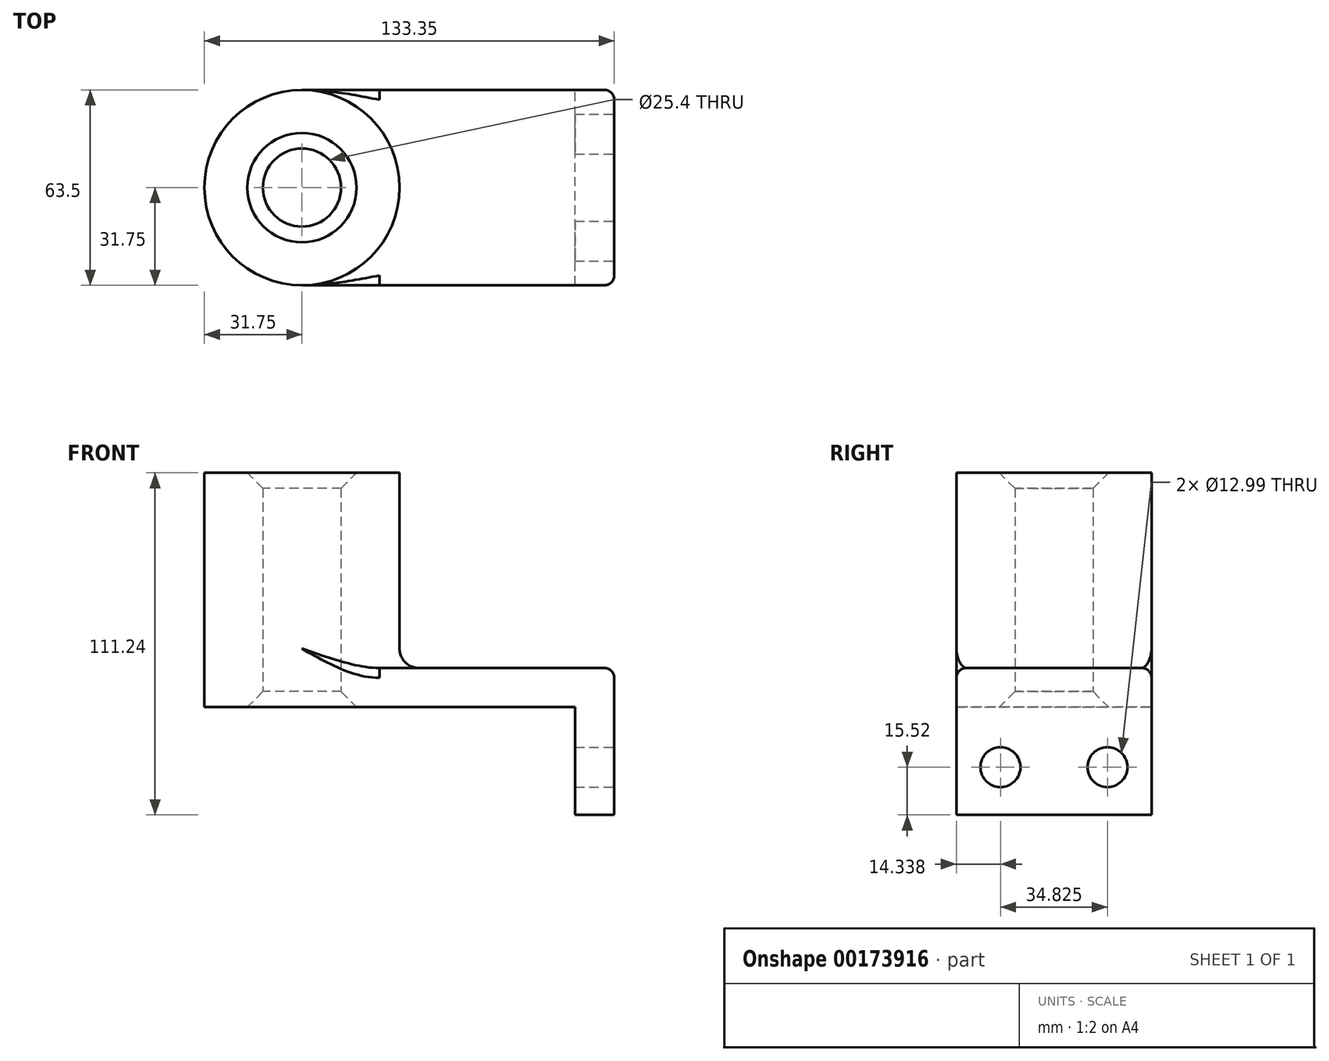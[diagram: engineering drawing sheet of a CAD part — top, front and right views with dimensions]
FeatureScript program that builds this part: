
annotation { "Feature Type Name" : "Feature", "Feature Type Description" : "" }
export const myFeature = defineFeature(function(context is Context, id is Id, definition is map)
    precondition{}
    {
        {
            var Q0;
            Q0=qCreatedBy(makeId("Top.planeOp"),FACE);
            var sketch = newSketch(context, id + "F0", { "sketchPlane" : qUnion([Q0])});
            skLineSegment(sketch, "E0.bottom", {"start": v(-50.8, 31.75) * mm, "end": v(50.8, 31.75) * mm});
            skLineSegment(sketch, "E0.top", {"start": v(-50.8, -31.75) * mm, "end": v(50.8, -31.75) * mm});
            skLineSegment(sketch, "E0.left", {"start": v(-50.8, 31.75) * mm, "end": v(-50.8, -31.75) * mm});
            skLineSegment(sketch, "E0.right", {"start": v(50.8, 31.75) * mm, "end": v(50.8, -31.75) * mm});
            skPoint(sketch, "E0.middle", {"position": v(0, 0) * mm});
            skCircle(sketch, "E1", {"center": v(-50.8, 0) * mm, "radius": 31.75 * mm});
            skCircle(sketch, "E2", {"center": v(-50.8, 0) * mm, "radius": 12.7 * mm});
            skSolve(sketch);
        }
        {
            var Q0;
            Q0 = qSketchRegion(id + "F0", true);
            extrude(context, id + "F1", {"entities" : qUnion([Q0]), "depth" : 12.7 * mm});
        }
        {
            var Q0;
            {var subQ1=sQuery(id+"F0.wireOp",EDGE,"E0.left");var subQ3=sQuery(id+"F0.wireOp",EDGE,"E2");var subQ4=makeQuery(id+"F0.imprint","INTERSECT",VERTEX,{"disambiguationData":[OD(0.0)],"derivedFrom":[subQ1,subQ3]});Q0=makeQuery(id+"F0.imprint","IMPRINT",FACE,{"disambiguationData":[TD([[makeQuery(id+"F0.imprint","IMPRINT",EDGE,{"disambiguationData":[TD([[subQ4,-1.0]])],"derivedFrom":subQ3}),-1.0]])]});}
            var Q1;
            {var subQ1=sQuery(id+"F0.wireOp",EDGE,"E0.left");var subQ3=sQuery(id+"F0.wireOp",EDGE,"E2");var subQ4=makeQuery(id+"F0.imprint","INTERSECT",VERTEX,{"disambiguationData":[OD(0.0)],"derivedFrom":[subQ1,subQ3]});Q1=makeQuery(id+"F0.imprint","IMPRINT",FACE,{"disambiguationData":[TD([[makeQuery(id+"F0.imprint","IMPRINT",EDGE,{"disambiguationData":[TD([[subQ4,1.0]])],"derivedFrom":subQ3}),-1.0]])]});}
            extrude(context, id + "F2", {"entities" : qUnion([Q0, Q1]), "operationType" : NewBodyOperationType.ADD, "depth" : 76.2 * mm});
        }
        {
            var Q0;
            Q0=makeQuery(id+"F1.opExtrude","SWEPT_FACE",FACE,{"disambiguationData":[OSD([sQuery(id+"F0.wireOp",EDGE,"E0.right")])]});
            var sketch = newSketch(context, id + "F3", { "sketchPlane" : qUnion([Q0])});
            skLineSegment(sketch, "E3.bottom", {"start": v(-31.75, 12.7) * mm, "end": v(31.75, 12.7) * mm});
            skLineSegment(sketch, "E3.top", {"start": v(-31.75, -35.04) * mm, "end": v(31.75, -35.04) * mm});
            skLineSegment(sketch, "E3.left", {"start": v(-31.75, 12.7) * mm, "end": v(-31.75, -35.04) * mm});
            skLineSegment(sketch, "E3.right", {"start": v(31.75, 12.7) * mm, "end": v(31.75, -35.04) * mm});
            skCircle(sketch, "E4", {"center": v(-17.41, -19.52) * mm, "radius": 6.5 * mm});
            skLineSegment(sketch, "E5", {"start": v(0, -35.04) * mm, "end": v(0, 52.12) * mm, "construction": true});
            skPoint(sketch, "E5.endSnap0", {"position": v(0, 0) * mm});
            skCircle(sketch, "E6.MirrorC", {"center": v(17.41, -19.52) * mm, "radius": 6.5 * mm});
            skSolve(sketch);
        }
        {
            var Q0;
            Q0 = qSketchRegion(id + "F3", true);
            extrude(context, id + "F4", {"entities" : qUnion([Q0]), "operationType" : NewBodyOperationType.ADD, "oppositeDirection" : true, "depth" : 12.7 * mm});
        }
        {
            var Q0;
            {var subQ0=sQuery(id+"F0.wireOp",EDGE,"E1");Q0=makeQuery(id+"F2.boolean.opBoolean","INTERSECT",EDGE,{"derivedFrom":[makeQuery(id+"F1.opExtrude","CAP_FACE",FACE,{"disambiguationData":[OSD([sQuery(id+"F0.wireOp",EDGE,"E0.bottom"),sQuery(id+"F0.wireOp",EDGE,"E0.top"),sQuery(id+"F0.wireOp",EDGE,"E0.right"),subQ0,sQuery(id+"F0.wireOp",EDGE,"E2")])],"isStart":false}),makeQuery(id+"F2.opExtrude","SWEPT_FACE",FACE,{"disambiguationData":[OSD([subQ0])]})]});}
            fillet(context, id + "F5", {"entities" : qUnion([Q0]), "radius" : 6.35 * mm, "tangentPropagation" : true, "allowEdgeOverflow" : false});
        }
        {
            var Q0;
            Q0=makeQuery(id+"F4.boolean.opBoolean","MERGE",EDGE,{"derivedFrom":[makeQuery(id+"F1.opExtrude","SWEPT_EDGE",EDGE,{"disambiguationData":[OSD([sQuery(id+"F0.wireOp",EDGE,"E0.top"),sQuery(id+"F0.wireOp",EDGE,"E0.right")])]}),makeQuery(id+"F4.opExtrude","CAP_EDGE",EDGE,{"disambiguationData":[OSD([sQuery(id+"F3.wireOp",EDGE,"E3.left")])],"isStart":true})]});
            var Q1;
            Q1=makeQuery(id+"F4.boolean.opBoolean","MERGE",EDGE,{"derivedFrom":[makeQuery(id+"F1.opExtrude","SWEPT_EDGE",EDGE,{"disambiguationData":[OSD([sQuery(id+"F0.wireOp",EDGE,"E0.bottom"),sQuery(id+"F0.wireOp",EDGE,"E0.right")])]}),makeQuery(id+"F4.opExtrude","CAP_EDGE",EDGE,{"disambiguationData":[OSD([sQuery(id+"F3.wireOp",EDGE,"E3.right")])],"isStart":true})]});
            fillet(context, id + "F6", {"entities" : qUnion([Q0, Q1]), "radius" : 3.17 * mm, "tangentPropagation" : true, "allowEdgeOverflow" : false});
        }
        {
            var Q0;
            Q0=makeQuery(id+"F1.opExtrude","CAP_EDGE",EDGE,{"disambiguationData":[OSD([sQuery(id+"F0.wireOp",EDGE,"E0.top")])],"isStart":false});
            var Q1;
            Q1=makeQuery(id+"F1.opExtrude","CAP_EDGE",EDGE,{"disambiguationData":[OSD([sQuery(id+"F0.wireOp",EDGE,"E0.bottom")])],"isStart":false});
            fillet(context, id + "F7", {"entities" : qUnion([Q0, Q1]), "radius" : 3.17 * mm, "tangentPropagation" : true, "allowEdgeOverflow" : false});
        }
        {
            var Q0;
            {var subQ0=sQuery(id+"F0.wireOp",EDGE,"E2");Q0=makeQuery(id+"F2.boolean.opBoolean","MERGE",FACE,{"derivedFrom":[makeQuery(id+"F1.opExtrude","SWEPT_FACE",FACE,{"disambiguationData":[OSD([subQ0])]}),makeQuery(id+"F2.opExtrude","SWEPT_FACE",FACE,{"disambiguationData":[OSD([subQ0])]})]});}
            chamfer(context, id + "F8", {"entities" : qUnion([Q0]), "width" : 5.08 * mm, "tangentPropagation" : true});
        }
    });
